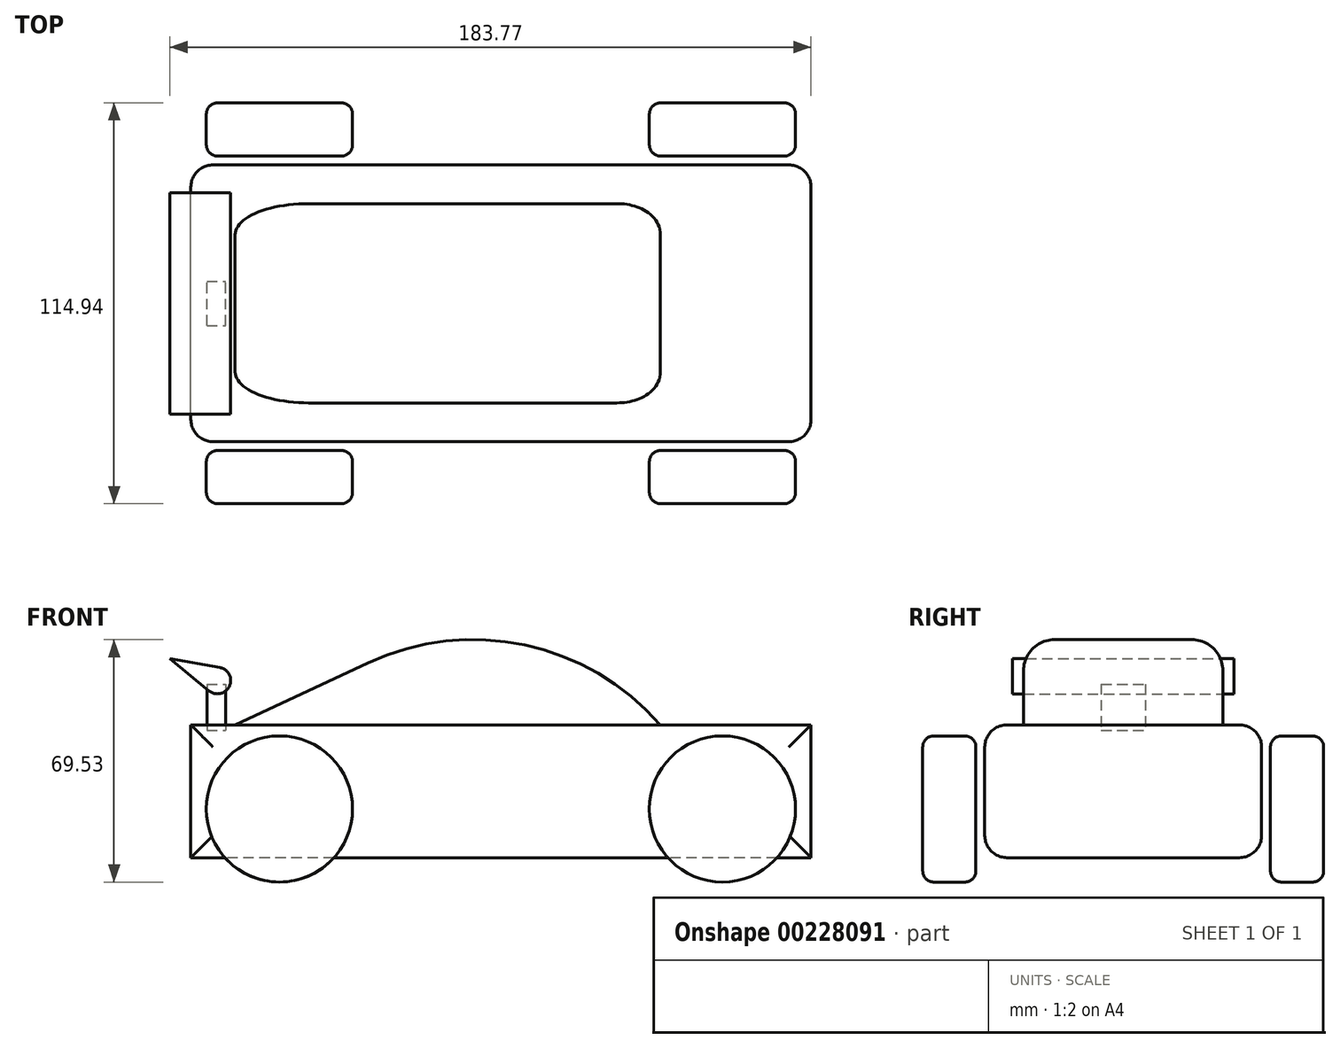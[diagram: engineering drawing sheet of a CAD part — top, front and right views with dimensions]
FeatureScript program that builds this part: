
annotation { "Feature Type Name" : "Feature", "Feature Type Description" : "" }
export const myFeature = defineFeature(function(context is Context, id is Id, definition is map)
    precondition{}
    {
        {
            var Q0;
            Q0=qCreatedBy(makeId("Front.planeOp"),FACE);
            var sketch = newSketch(context, id + "F0", { "sketchPlane" : qUnion([Q0])});
            skLineSegment(sketch, "E0.bottom", {"start": v(88.9, 19.05) * mm, "end": v(-88.9, 19.05) * mm});
            skLineSegment(sketch, "E0.top", {"start": v(88.9, -19.05) * mm, "end": v(-88.9, -19.05) * mm});
            skLineSegment(sketch, "E0.left", {"start": v(88.9, 19.05) * mm, "end": v(88.9, -19.05) * mm});
            skLineSegment(sketch, "E0.right", {"start": v(-88.9, 19.05) * mm, "end": v(-88.9, -19.05) * mm});
            skPoint(sketch, "E0.middle", {"position": v(0, 0) * mm});
            skLineSegment(sketch, "E1", {"start": v(-99.22, -26.04) * mm, "end": v(97.95, -26.04) * mm, "construction": true});
            skCircle(sketch, "E2", {"center": v(63.5, -5.08) * mm, "radius": 20.96 * mm});
            skSolve(sketch);
        }
        {
            var Q0;
            Q0=qCreatedBy(makeId("Front.planeOp"),FACE);
            var sketch = newSketch(context, id + "F1", { "sketchPlane" : qUnion([Q0])});
            skLineSegment(sketch, "E3.0", {"start": v(88.9, 19.05) * mm, "end": v(-88.9, 19.05) * mm});
            skLineSegment(sketch, "E4.0", {"start": v(-88.9, 19.05) * mm, "end": v(-88.9, -19.05) * mm});
            skLineSegment(sketch, "E5.0", {"start": v(88.9, -19.05) * mm, "end": v(-88.9, -19.05) * mm});
            skLineSegment(sketch, "E6.0", {"start": v(88.9, 19.05) * mm, "end": v(88.9, -19.05) * mm});
            skSolve(sketch);
        }
        {
            var Q0;
            Q0=makeQuery(id+"F1.imprint","IMPRINT",FACE,{"disambiguationData":[TD([[makeQuery(id+"F1.imprint","IMPRINT",EDGE,{"derivedFrom":sQuery(id+"F1.wireOp",EDGE,"E3.0")}),1.0]])]});
            extrude(context, id + "F2", {"entities" : qUnion([Q0]), "depth" : 79.38 * mm, "symmetric" : true});
        }
        {
            var Q0;
            Q0=makeQuery(id+"F2.opExtrude","CAP_FACE",FACE,{"disambiguationData":[OSD([sQuery(id+"F1.wireOp",EDGE,"E3.0"),sQuery(id+"F1.wireOp",EDGE,"E4.0"),sQuery(id+"F1.wireOp",EDGE,"E5.0"),sQuery(id+"F1.wireOp",EDGE,"E6.0")])],"isStart":false});
            cPlane(context, id + "F3", {"entities" : qUnion([Q0]), "cplaneType" : CPlaneType.OFFSET, "offset" : 2.54 * mm, "width" : 152.4 * mm, "height" : 152.4 * mm});
        }
        {
            var Q0;
            Q0=qCreatedBy(id+"F3.planeOp",FACE);
            var sketch = newSketch(context, id + "F4", { "sketchPlane" : qUnion([Q0])});
            skCircle(sketch, "E7.0", {"center": v(63.5, -5.08) * mm, "radius": 20.96 * mm});
            skSolve(sketch);
        }
        {
            var Q0;
            Q0 = qSketchRegion(id + "F4", true);
            extrude(context, id + "F5", {"entities" : qUnion([Q0]), "depth" : 15.24 * mm});
        }
        {
            var Q0;
            Q0=makeQuery(id+"F2.opExtrude","CAP_FACE",FACE,{"disambiguationData":[OSD([sQuery(id+"F1.wireOp",EDGE,"E3.0"),sQuery(id+"F1.wireOp",EDGE,"E4.0"),sQuery(id+"F1.wireOp",EDGE,"E5.0"),sQuery(id+"F1.wireOp",EDGE,"E6.0")])],"isStart":false});
            var Q1;
            Q1=makeQuery(id+"F2.opExtrude","CAP_FACE",FACE,{"disambiguationData":[OSD([sQuery(id+"F1.wireOp",EDGE,"E3.0"),sQuery(id+"F1.wireOp",EDGE,"E4.0"),sQuery(id+"F1.wireOp",EDGE,"E5.0"),sQuery(id+"F1.wireOp",EDGE,"E6.0")])],"isStart":true});
            fillet(context, id + "F6", {"entities" : qUnion([Q0, Q1]), "radius" : 6.35 * mm, "tangentPropagation" : true, "allowEdgeOverflow" : false});
        }
        {
            var Q0;
            Q0=makeQuery(id+"F5.opExtrude","SWEPT_FACE",FACE,{"disambiguationData":[OSD([sQuery(id+"F4.wireOp",EDGE,"E7.0")])]});
            fillet(context, id + "F7", {"entities" : qUnion([Q0]), "radius" : 3.17 * mm, "tangentPropagation" : true, "allowEdgeOverflow" : false});
        }
        {
            var Q0;
            Q0=makeQuery(id+"F5.opExtrude","SWEPT_BODY",BODY,{"disambiguationData":[OSD([sQuery(id+"F4.wireOp",EDGE,"E7.0")])]});
            var Q1;
            Q1=qCreatedBy(makeId("Front.planeOp"),FACE);
            mirror(context, id + "F8", {"entities" : qUnion([Q0]), "mirrorPlane" : qUnion([Q1])});
        }
        {
            var Q0;
            Q0=makeQuery(id+"F8.opPattern","COPY",BODY,{"derivedFrom":makeQuery(id+"F5.opExtrude","SWEPT_BODY",BODY,{"disambiguationData":[OSD([sQuery(id+"F4.wireOp",EDGE,"E7.0")])]}),"instanceName":"1"});
            var Q1;
            Q1=makeQuery(id+"F5.opExtrude","SWEPT_BODY",BODY,{"disambiguationData":[OSD([sQuery(id+"F4.wireOp",EDGE,"E7.0")])]});
            var Q2;
            Q2=qCreatedBy(makeId("Right.planeOp"),FACE);
            mirror(context, id + "F9", {"entities" : qUnion([Q0, Q1]), "mirrorPlane" : qUnion([Q2])});
        }
        {
            var Q0;
            Q0=qCreatedBy(makeId("Front.planeOp"),FACE);
            var sketch = newSketch(context, id + "F10", { "sketchPlane" : qUnion([Q0])});
            skLineSegment(sketch, "E8", {"start": v(-76.2, 19.05) * mm, "end": v(45.72, 19.05) * mm});
            skLineSegment(sketch, "E9", {"start": v(-76.2, 19.05) * mm, "end": v(-38.1, 36.82) * mm});
            skArc(sketch, "E10", {"start": v(-38.1, 36.82) * mm, "mid": v(6.78, 41.94) * mm, "end": v(45.72, 19.05) * mm});
            skSolve(sketch);
        }
        {
            var Q0;
            Q0 = qSketchRegion(id + "F10", true);
            extrude(context, id + "F11", {"entities" : qUnion([Q0]), "operationType" : NewBodyOperationType.ADD, "depth" : 57.15 * mm, "symmetric" : true});
        }
        {
            var Q0;
            Q0=makeQuery(id+"F11.opExtrude","CAP_EDGE",EDGE,{"disambiguationData":[OSD([sQuery(id+"F10.wireOp",EDGE,"E9")])],"isStart":true});
            var Q1;
            Q1=makeQuery(id+"F11.opExtrude","CAP_EDGE",EDGE,{"disambiguationData":[OSD([sQuery(id+"F10.wireOp",EDGE,"E10")])],"isStart":true});
            var Q2;
            Q2=makeQuery(id+"F11.opExtrude","CAP_EDGE",EDGE,{"disambiguationData":[OSD([sQuery(id+"F10.wireOp",EDGE,"E9")])],"isStart":false});
            var Q3;
            Q3=makeQuery(id+"F11.opExtrude","CAP_EDGE",EDGE,{"disambiguationData":[OSD([sQuery(id+"F10.wireOp",EDGE,"E10")])],"isStart":false});
            fillet(context, id + "F12", {"entities" : qUnion([Q0, Q1, Q2, Q3]), "radius" : 8.9 * mm, "tangentPropagation" : true, "allowEdgeOverflow" : false});
        }
        {
            var Q0;
            Q0=qCreatedBy(makeId("Front.planeOp"),FACE);
            var sketch = newSketch(context, id + "F13", { "sketchPlane" : qUnion([Q0])});
            skLineSegment(sketch, "E11", {"start": v(-94.87, 38.1) * mm, "end": v(-80.6, 35.5) * mm});
            skLineSegment(sketch, "E12", {"start": v(-94.87, 38.1) * mm, "end": v(-83.72, 28.82) * mm});
            skArc(sketch, "E13", {"start": v(-83.72, 28.82) * mm, "mid": v(-77.83, 30.14) * mm, "end": v(-80.6, 35.5) * mm});
            skSolve(sketch);
        }
        {
            var Q0;
            Q0 = qSketchRegion(id + "F13", true);
            extrude(context, id + "F14", {"entities" : qUnion([Q0]), "depth" : 63.5 * mm, "symmetric" : true});
        }
        {
            var Q0;
            Q0=qCreatedBy(makeId("Front.planeOp"),FACE);
            var sketch = newSketch(context, id + "F15", { "sketchPlane" : qUnion([Q0])});
            skLineSegment(sketch, "E14.bottom", {"start": v(-84.3, 30.73) * mm, "end": v(-78.96, 30.73) * mm});
            skLineSegment(sketch, "E14.top", {"start": v(-84.3, 17.41) * mm, "end": v(-78.96, 17.41) * mm});
            skLineSegment(sketch, "E14.left", {"start": v(-84.3, 30.73) * mm, "end": v(-84.3, 17.41) * mm});
            skLineSegment(sketch, "E14.right", {"start": v(-78.96, 30.73) * mm, "end": v(-78.96, 17.41) * mm});
            skSolve(sketch);
        }
        {
            var Q0;
            Q0 = qSketchRegion(id + "F15", true);
            extrude(context, id + "F16", {"entities" : qUnion([Q0]), "depth" : 12.7 * mm, "symmetric" : true});
        }
    });
